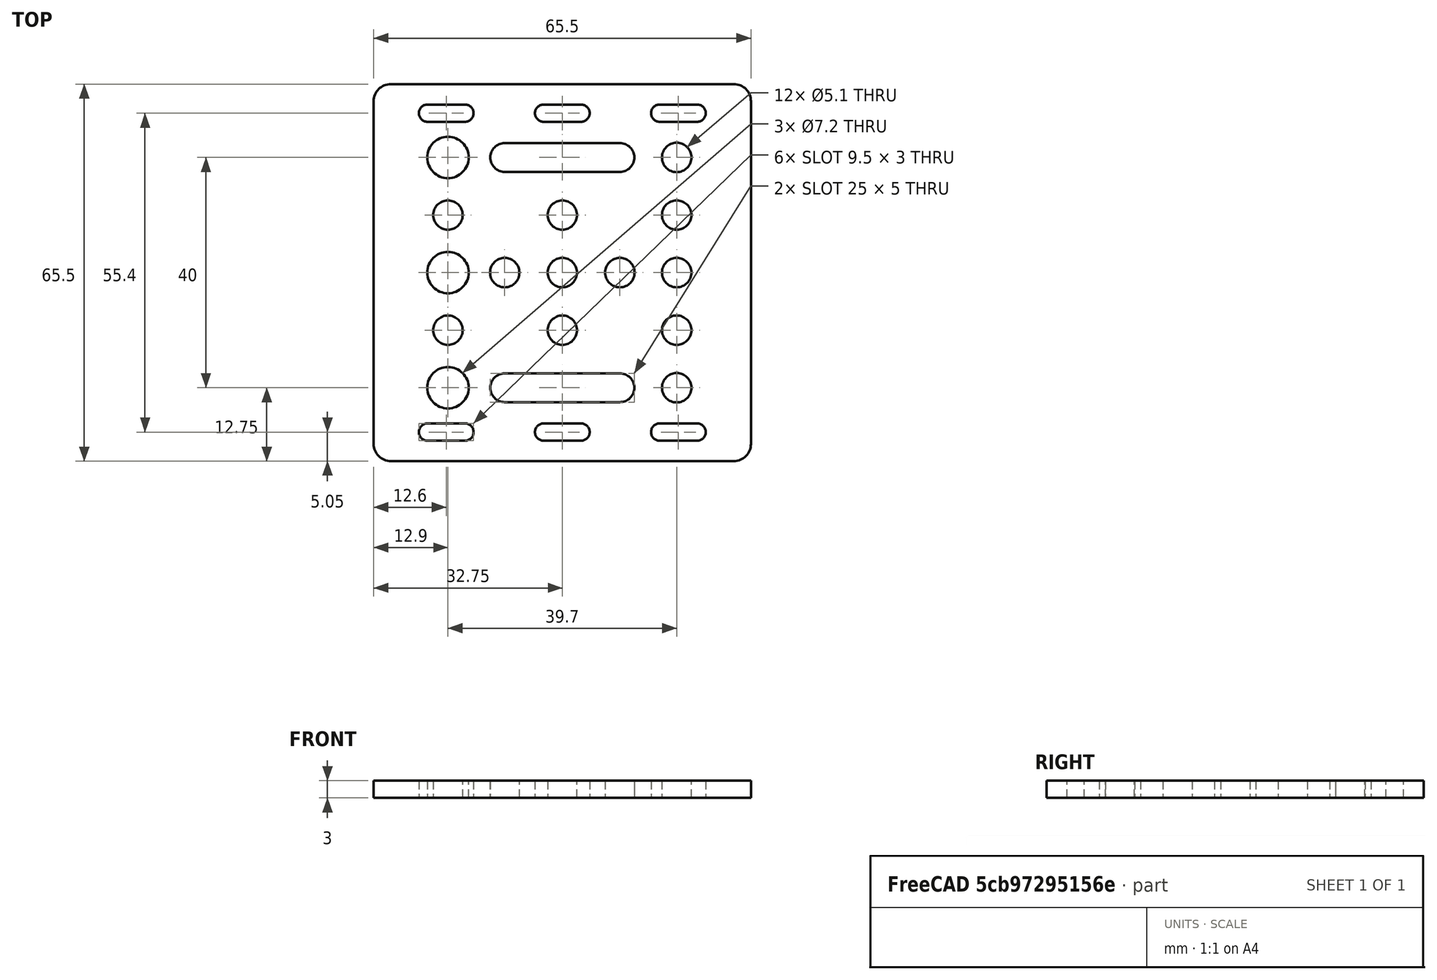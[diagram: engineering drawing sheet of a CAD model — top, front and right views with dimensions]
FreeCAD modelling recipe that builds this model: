
FCSTD DOCUMENT  (FreeCAD 0.18.4R)
Label: V-Slot_20mm
License: All rights reserved
LicenseURL: http://en.wikipedia.org/wiki/All_rights_reserved
objects: Sketcher::SketchObject×1, PartDesign::Pad×1, PartDesign::Body×1
note: 4 computed .brp shape members not serialized (recipe doc carries the construction recipe); baked Part::Feature solids carry a one-line shape summary decoded from their .brp

FEATURE [Sketcher::SketchObject] Sketch
  MapMode = 5
  Support = -> [XY_Plane]
  sketch-geometry (55):
    g0: LineSegment StartX=-29.75 StartY=32.75 StartZ=0 EndX=29.75 EndY=32.75 EndZ=0
    g1: LineSegment StartX=32.75 StartY=29.75 StartZ=0 EndX=32.75 EndY=-29.75 EndZ=0
    g2: LineSegment StartX=29.75 StartY=-32.75 StartZ=0 EndX=-29.75 EndY=-32.75 EndZ=0
    g3: LineSegment StartX=-32.75 StartY=-29.75 StartZ=0 EndX=-32.75 EndY=29.75 EndZ=0
    g4: Circle CenterX=-19.85 CenterY=20 CenterZ=0 NormalX=0 NormalY=0 NormalZ=1 AngleXU=0 Radius=3.6
    g5: Circle CenterX=-19.85 CenterY=-20 CenterZ=0 NormalX=0 NormalY=0 NormalZ=1 AngleXU=0 Radius=3.6
    g6: Circle CenterX=-19.85 CenterY=-10 CenterZ=0 NormalX=0 NormalY=0 NormalZ=1 AngleXU=0 Radius=2.55
    g7: Circle CenterX=-19.85 CenterY=10 CenterZ=0 NormalX=0 NormalY=0 NormalZ=1 AngleXU=0 Radius=2.55
    g8: Circle CenterX=-19.85 CenterY=0 CenterZ=0 NormalX=0 NormalY=0 NormalZ=1 AngleXU=0 Radius=3.6
    g9: Circle CenterX=19.85 CenterY=20 CenterZ=0 NormalX=0 NormalY=0 NormalZ=1 AngleXU=0 Radius=2.55
    g10: Circle CenterX=19.85 CenterY=10 CenterZ=0 NormalX=0 NormalY=0 NormalZ=1 AngleXU=0 Radius=2.55
    g11: Circle CenterX=19.85 CenterY=1.6e-15 CenterZ=0 NormalX=0 NormalY=0 NormalZ=1 AngleXU=0 Radius=2.55
    g12: Circle CenterX=19.85 CenterY=-20 CenterZ=0 NormalX=0 NormalY=0 NormalZ=1 AngleXU=0 Radius=2.55
    g13: Circle CenterX=19.85 CenterY=-10 CenterZ=0 NormalX=0 NormalY=0 NormalZ=1 AngleXU=0 Radius=2.55
    g14: Circle CenterX=0 CenterY=0 CenterZ=0 NormalX=0 NormalY=0 NormalZ=1 AngleXU=0 Radius=2.55
    g15: Circle CenterX=0 CenterY=10 CenterZ=0 NormalX=0 NormalY=0 NormalZ=1 AngleXU=0 Radius=2.55
    g16: Circle CenterX=0 CenterY=-10 CenterZ=0 NormalX=0 NormalY=0 NormalZ=1 AngleXU=0 Radius=2.55
    g17: Circle CenterX=10 CenterY=0 CenterZ=0 NormalX=0 NormalY=0 NormalZ=1 AngleXU=0 Radius=2.55
    g18: Circle CenterX=-10 CenterY=0 CenterZ=0 NormalX=0 NormalY=0 NormalZ=1 AngleXU=0 Radius=2.55
    g19: ArcOfCircle CenterX=-10 CenterY=-20 CenterZ=0 NormalX=0 NormalY=0 NormalZ=1 AngleXU=0 Radius=2.5 StartAngle=1.5708 EndAngle=4.71239
    g20: ArcOfCircle CenterX=10 CenterY=-20 CenterZ=0 NormalX=0 NormalY=0 NormalZ=1 AngleXU=0 Radius=2.5 StartAngle=4.71239 EndAngle=7.85398
    g21: LineSegment StartX=-10 StartY=-22.5 StartZ=0 EndX=10 EndY=-22.5 EndZ=0
    g22: LineSegment StartX=-10 StartY=-17.5 StartZ=0 EndX=10 EndY=-17.5 EndZ=0
    g23: ArcOfCircle CenterX=-10 CenterY=20 CenterZ=0 NormalX=0 NormalY=0 NormalZ=1 AngleXU=0 Radius=2.5 StartAngle=1.5708 EndAngle=4.71239
    g24: ArcOfCircle CenterX=10 CenterY=20 CenterZ=0 NormalX=0 NormalY=0 NormalZ=1 AngleXU=0 Radius=2.5 StartAngle=4.71239 EndAngle=7.85398
    g25: LineSegment StartX=-10 StartY=17.5 StartZ=0 EndX=10 EndY=17.5 EndZ=0
    g26: LineSegment StartX=-10 StartY=22.5 StartZ=0 EndX=10 EndY=22.5 EndZ=0
    g27: ArcOfCircle CenterX=-23.4 CenterY=-27.7 CenterZ=0 NormalX=0 NormalY=0 NormalZ=1 AngleXU=0 Radius=1.5 StartAngle=1.5708 EndAngle=4.71239
    g28: ArcOfCircle CenterX=-16.9 CenterY=-27.7 CenterZ=0 NormalX=0 NormalY=0 NormalZ=1 AngleXU=0 Radius=1.5 StartAngle=4.71239 EndAngle=7.85398
    g29: LineSegment StartX=-23.4 StartY=-29.2 StartZ=0 EndX=-16.9 EndY=-29.2 EndZ=0
    g30: LineSegment StartX=-23.4 StartY=-26.2 StartZ=0 EndX=-16.9 EndY=-26.2 EndZ=0
    g31: ArcOfCircle CenterX=-3.25 CenterY=-27.7 CenterZ=0 NormalX=0 NormalY=0 NormalZ=1 AngleXU=0 Radius=1.5 StartAngle=1.5708 EndAngle=4.71239
    g32: ArcOfCircle CenterX=3.25 CenterY=-27.7 CenterZ=0 NormalX=0 NormalY=0 NormalZ=1 AngleXU=0 Radius=1.5 StartAngle=4.71239 EndAngle=7.85398
    g33: LineSegment StartX=-3.25 StartY=-29.2 StartZ=0 EndX=3.25 EndY=-29.2 EndZ=0
    g34: LineSegment StartX=-3.25 StartY=-26.2 StartZ=0 EndX=3.25 EndY=-26.2 EndZ=0
    g35: ArcOfCircle CenterX=16.9 CenterY=-27.7 CenterZ=0 NormalX=0 NormalY=0 NormalZ=1 AngleXU=0 Radius=1.5 StartAngle=1.5708 EndAngle=4.71239
    g36: ArcOfCircle CenterX=23.4 CenterY=-27.7 CenterZ=0 NormalX=0 NormalY=0 NormalZ=1 AngleXU=0 Radius=1.5 StartAngle=4.71239 EndAngle=7.85398
    g37: LineSegment StartX=16.9 StartY=-29.2 StartZ=0 EndX=23.4 EndY=-29.2 EndZ=0
    g38: LineSegment StartX=16.9 StartY=-26.2 StartZ=0 EndX=23.4 EndY=-26.2 EndZ=0
    g39: ArcOfCircle CenterX=-23.4 CenterY=27.7 CenterZ=0 NormalX=0 NormalY=0 NormalZ=1 AngleXU=0 Radius=1.5 StartAngle=1.5708 EndAngle=4.71239
    g40: ArcOfCircle CenterX=-16.9 CenterY=27.7 CenterZ=0 NormalX=0 NormalY=0 NormalZ=1 AngleXU=0 Radius=1.5 StartAngle=4.71239 EndAngle=7.85398
    g41: LineSegment StartX=-23.4 StartY=26.2 StartZ=0 EndX=-16.9 EndY=26.2 EndZ=0
    g42: LineSegment StartX=-23.4 StartY=29.2 StartZ=0 EndX=-16.9 EndY=29.2 EndZ=0
    g43: ArcOfCircle CenterX=-3.25 CenterY=27.7 CenterZ=0 NormalX=0 NormalY=0 NormalZ=1 AngleXU=0 Radius=1.5 StartAngle=1.5708 EndAngle=4.71239
    g44: ArcOfCircle CenterX=3.25 CenterY=27.7 CenterZ=0 NormalX=0 NormalY=0 NormalZ=1 AngleXU=0 Radius=1.5 StartAngle=4.71239 EndAngle=7.85398
    g45: LineSegment StartX=-3.25 StartY=26.2 StartZ=0 EndX=3.25 EndY=26.2 EndZ=0
    g46: LineSegment StartX=-3.25 StartY=29.2 StartZ=0 EndX=3.25 EndY=29.2 EndZ=0
    g47: ArcOfCircle CenterX=16.9 CenterY=27.7 CenterZ=0 NormalX=0 NormalY=0 NormalZ=1 AngleXU=0 Radius=1.5 StartAngle=1.5708 EndAngle=4.71239
    g48: ArcOfCircle CenterX=23.4 CenterY=27.7 CenterZ=0 NormalX=0 NormalY=0 NormalZ=1 AngleXU=0 Radius=1.5 StartAngle=4.71239 EndAngle=7.85398
    g49: LineSegment StartX=16.9 StartY=26.2 StartZ=0 EndX=23.4 EndY=26.2 EndZ=0
    g50: LineSegment StartX=16.9 StartY=29.2 StartZ=0 EndX=23.4 EndY=29.2 EndZ=0
    g51: ArcOfCircle CenterX=-29.75 CenterY=29.75 CenterZ=0 NormalX=0 NormalY=0 NormalZ=1 AngleXU=0 Radius=3 StartAngle=1.5708 EndAngle=3.14159
    g52: ArcOfCircle CenterX=29.75 CenterY=29.75 CenterZ=0 NormalX=0 NormalY=0 NormalZ=1 AngleXU=0 Radius=3 StartAngle=-9e-16 EndAngle=1.5708
    g53: ArcOfCircle CenterX=29.75 CenterY=-29.75 CenterZ=0 NormalX=0 NormalY=0 NormalZ=1 AngleXU=0 Radius=3 StartAngle=4.71239 EndAngle=6.28319
    g54: ArcOfCircle CenterX=-29.75 CenterY=-29.75 CenterZ=0 NormalX=0 NormalY=0 NormalZ=1 AngleXU=0 Radius=3 StartAngle=3.14159 EndAngle=4.71239
  constraints (144):
    c: Horizontal(g0)
    c: Horizontal(g2)
    c: Vertical(g1)
    c: Distance(g-1,g0) = 32.75
    c: Equal(g0,g3)
    c: Distance(g4,g3) = 12.9
    c: Distance(g7,g3) = 12.9
    c: Distance(g8,g3) = 12.9
    c: Distance(g6,g3) = 12.9
    c: Distance(g5,g3) = 12.9
    c: Perpendicular(g0,g3)
    c: PointOnObject(g8,g-1)
    c: Diameter(g4) = 7.2
    c: Diameter(g5) = 7.2
    c: Diameter(g8) = 7.2
    c: Diameter(g7) = 5.1
    c: Diameter(g6) = 5.1
    c: Distance(g5,g0) = 52.75
    c: Distance(g4,g0) = 12.75
    c: Distance(g7,g0) = 22.75
    c: Distance(g6,g0) = 42.75
    c: Diameter(g9) = 5.1
    c: Diameter(g10) = 5.1
    c: Diameter(g11) = 5.1
    c: Diameter(g13) = 5.1
    c: Diameter(g12) = 5.1
    c: Distance(g9,g1) = 12.9
    c: Distance(g10,g1) = 12.9
    c: Distance(g11,g1) = 12.9
    c: Distance(g13,g1) = 12.9
    c: Distance(g12,g1) = 12.9
    c: Distance(g9,g0) = 12.75
    c: Distance(g10,g0) = 22.75
    c: Distance(g11,g0) = 32.75
    c: Distance(g13,g0) = 42.75
    c: Distance(g12,g0) = 52.75
    c: Diameter(g14) = 5.1
    c: Diameter(g16) = 5.1
    c: Diameter(g15) = 5.1
    c: Diameter(g18) = 5.1
    c: Diameter(g17) = 5.1
    c: Coincident(g14,g-1)
    c: PointOnObject(g15,g-2)
    c: PointOnObject(g16,g-2)
    c: PointOnObject(g18,g-1)
    c: PointOnObject(g17,g-1)
    c: Distance(g16,g0) = 42.75
    c: Distance(g15,g0) = 22.75
    c: Distance(g18,g3) = 22.75
    c: Distance(g17,g1) = 22.75
    c: Tangent(g19,g22) = 1.5708
    c: Tangent(g19,g21) = -1.5708
    c: Tangent(g21,g20) = -1.5708
    c: Tangent(g22,g20) = 1.5708
    c: Horizontal(g21)
    c: Equal(g19,g20)
    c: Tangent(g23,g26) = 1.5708
    c: Tangent(g23,g25) = -1.5708
    c: Tangent(g25,g24) = -1.5708
    c: Tangent(g26,g24) = 1.5708
    c: Horizontal(g25)
    c: Equal(g23,g24)
    c: Distance(g20,g20) = 5
    c: Distance(g24,g24) = 5
    c: Distance(g23,g3) = 22.75
    c: Distance(g24,g1) = 22.75
    c: Distance(g23,g0) = 10.25
    c: Distance(g19,g2) = 10.25
    c: Distance(g21) = 20
    c: Distance(g19,g3) = 22.75
    c: Tangent(g27,g30) = 1.5708
    c: Tangent(g27,g29) = -1.5708
    c: Tangent(g29,g28) = -1.5708
    c: Tangent(g30,g28) = 1.5708
    c: Horizontal(g29)
    c: Equal(g27,g28)
    c: Distance(g27,g27) = 3
    c: Distance(g27,g3) = 9.35
    c: Distance(g28,g3) = 15.85
    c: Distance(g27,g0) = 58.95
    c: Tangent(g31,g34) = 1.5708
    c: Tangent(g31,g33) = -1.5708
    c: Tangent(g33,g32) = -1.5708
    c: Tangent(g34,g32) = 1.5708
    c: Horizontal(g33)
    c: Equal(g31,g32)
    c: Tangent(g35,g38) = 1.5708
    c: Tangent(g35,g37) = -1.5708
    c: Tangent(g37,g36) = -1.5708
    c: Tangent(g38,g36) = 1.5708
    c: Horizontal(g37)
    c: Equal(g35,g36)
    c: Distance(g31,g31) = 3
    c: Distance(g35,g35) = 3
    c: Distance(g31,g3) = 29.5
    c: Distance(g32,g3) = 36
    c: Distance(g35,g3) = 49.65
    c: Distance(g36,g3) = 56.15
    c: Distance(g32,g0) = 58.95
    c: Distance(g36,g0) = 58.95
    c: Tangent(g39,g42) = 1.5708
    c: Tangent(g39,g41) = -1.5708
    c: Tangent(g41,g40) = -1.5708
    c: Tangent(g42,g40) = 1.5708
    c: Horizontal(g41)
    c: Equal(g39,g40)
    c: Tangent(g43,g46) = 1.5708
    c: Tangent(g43,g45) = -1.5708
    c: Tangent(g45,g44) = -1.5708
    c: Tangent(g46,g44) = 1.5708
    c: Horizontal(g45)
    c: Equal(g43,g44)
    c: Tangent(g47,g50) = 1.5708
    c: Tangent(g47,g49) = -1.5708
    c: Tangent(g49,g48) = -1.5708
    c: Tangent(g50,g48) = 1.5708
    c: Horizontal(g49)
    c: Equal(g47,g48)
    c: Distance(g39,g39) = 3
    c: Distance(g43,g43) = 3
    c: Distance(g47,g47) = 3
    c: Distance(g39,g3) = 9.35
    c: Distance(g40,g3) = 15.85
    c: Distance(g43,g3) = 29.5
    c: Distance(g44,g3) = 36
    c: Distance(g47,g3) = 49.65
    c: Distance(g48,g3) = 56.15
    c: Distance(g39,g0) = 3.55
    c: Distance(g43,g0) = 3.55
    c: Distance(g47,g0) = 3.55
    c: Tangent(g3,g51) = 1.5708
    c: Tangent(g0,g51) = 1.5708
    c: Tangent(g0,g52) = 1.5708
    c: Tangent(g1,g52) = 1.5708
    c: Tangent(g2,g53) = 1.5708
    c: Tangent(g1,g53) = 1.5708
    c: Tangent(g2,g54) = 1.5708
    c: Tangent(g3,g54) = 1.5708
    c: Radius(g53) = 3
    c: Radius(g54) = 3
    c: Radius(g51) = 3
    c: Radius(g52) = 3
    c: Distance(g0,g2) = 65.5
    c: Distance(g3,g-2) = 32.75
FEATURE [PartDesign::Pad] Pad
  Length = 3
  Length2 = 100
  Profile = -> Sketch
  Type = 0
FEATURE [PartDesign::Body] Body  label="gantry plate"
  Group = -> [Sketch,Pad]
  Origin = -> Origin
  Tip = -> Pad
